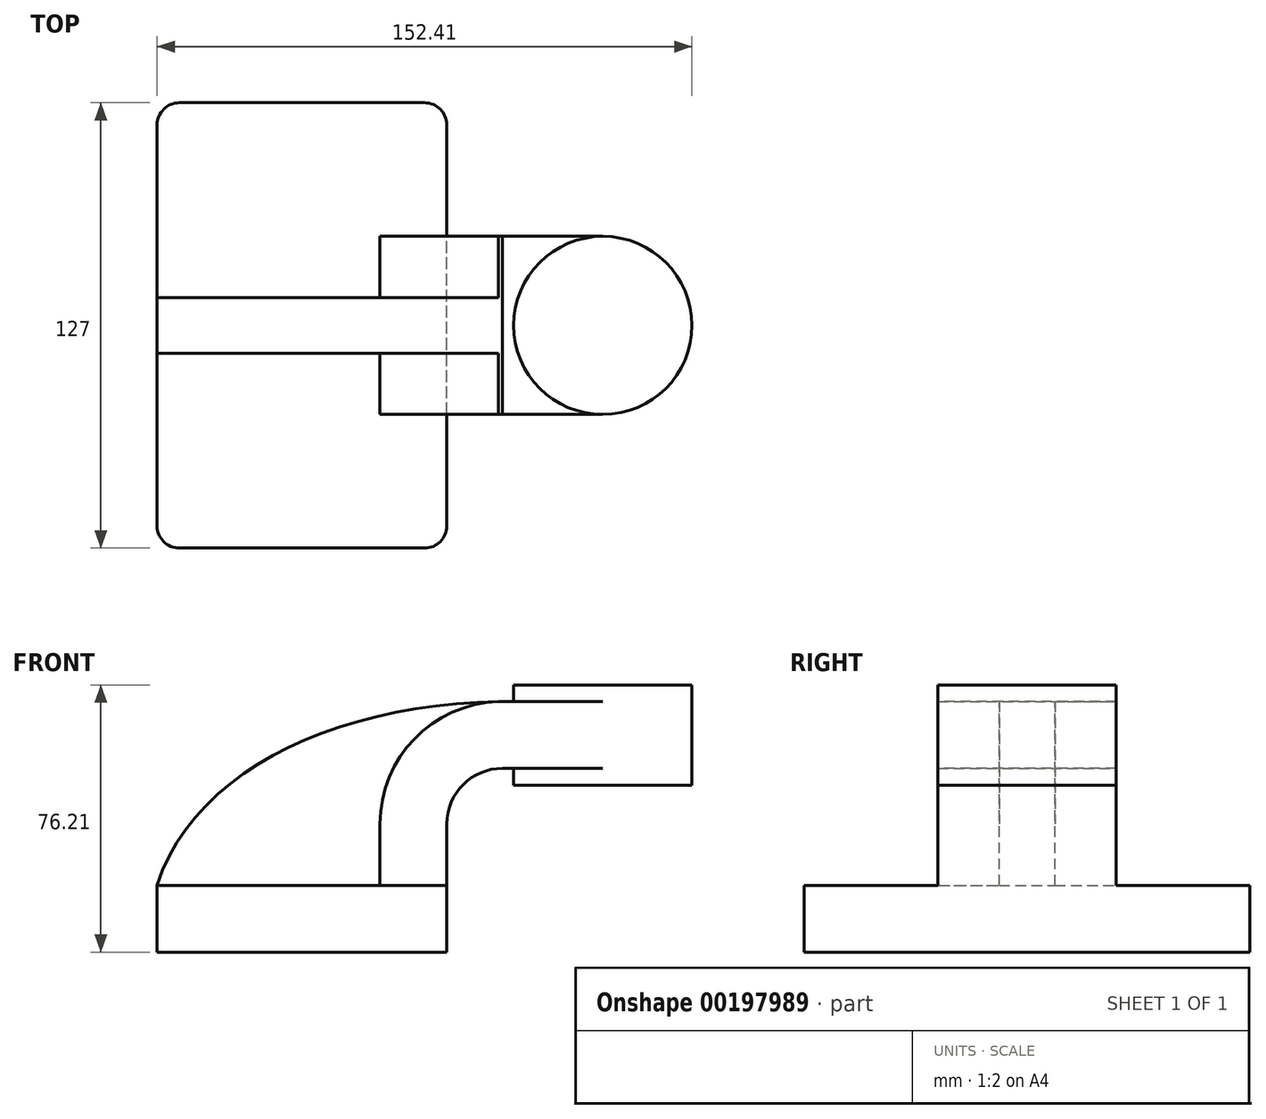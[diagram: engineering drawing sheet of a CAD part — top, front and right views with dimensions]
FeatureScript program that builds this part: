
annotation { "Feature Type Name" : "Feature", "Feature Type Description" : "" }
export const myFeature = defineFeature(function(context is Context, id is Id, definition is map)
    precondition{}
    {
        {
            var Q0;
            Q0=qCreatedBy(makeId("Front.planeOp"),FACE);
            var sketch = newSketch(context, id + "F0", { "sketchPlane" : qUnion([Q0])});
            skLineSegment(sketch, "E0.bottom", {"start": v(-41.28, 9.52) * mm, "end": v(41.28, 9.52) * mm});
            skLineSegment(sketch, "E0.top", {"start": v(-41.27, -9.53) * mm, "end": v(41.28, -9.53) * mm});
            skLineSegment(sketch, "E0.left", {"start": v(-41.28, 9.52) * mm, "end": v(-41.28, -9.53) * mm});
            skLineSegment(sketch, "E0.right", {"start": v(41.27, 9.53) * mm, "end": v(41.28, -9.52) * mm});
            skPoint(sketch, "E0.middle", {"position": v(0, 0) * mm});
            skLineSegment(sketch, "E1.bottom", {"start": v(111.12, 38.1) * mm, "end": v(60.32, 38.1) * mm});
            skLineSegment(sketch, "E1.top", {"start": v(111.12, 66.68) * mm, "end": v(60.32, 66.68) * mm});
            skLineSegment(sketch, "E1.left", {"start": v(111.12, 38.1) * mm, "end": v(111.12, 66.68) * mm});
            skLineSegment(sketch, "E1.right", {"start": v(60.32, 38.1) * mm, "end": v(60.32, 66.68) * mm});
            skPoint(sketch, "E1.middle", {"position": v(85.72, 52.39) * mm});
            skLineSegment(sketch, "E2", {"start": v(41.27, 9.53) * mm, "end": v(41.27, 27) * mm});
            skArc(sketch, "E3", {"start": v(41.27, 27) * mm, "mid": v(45.92, 38.23) * mm, "end": v(57.15, 42.88) * mm});
            skLineSegment(sketch, "E4", {"start": v(57.15, 42.88) * mm, "end": v(85.72, 42.88) * mm});
            skLineSegment(sketch, "E5.0", {"start": v(57.15, 61.93) * mm, "end": v(85.72, 61.93) * mm});
            skArc(sketch, "E5.1", {"start": v(22.22, 27) * mm, "mid": v(32.45, 51.7) * mm, "end": v(57.15, 61.93) * mm});
            skLineSegment(sketch, "E5.2", {"start": v(22.22, 9.52) * mm, "end": v(22.22, 27) * mm});
            skFitSpline(sketch, "E6", {"points": [v(-41.28, 9.53) * mm, v(57.15, 61.93) * mm], "startDerivative": vector(31.82, 99.3) * mm, "endDerivative": vector(140.95, 1.9) * mm});
            skLineSegment(sketch, "E7", {"start": v(85.72, 66.68) * mm, "end": v(85.72, 38.1) * mm});
            skSolve(sketch);
        }
        {
            var Q0;
            Q0=makeQuery(id+"F0.imprint","IMPRINT",FACE,{"disambiguationData":[TD([[makeQuery(id+"F0.imprint","IMPRINT",EDGE,{"derivedFrom":sQuery(id+"F0.wireOp",EDGE,"E0.top")}),1.0]])]});
            extrude(context, id + "F1", {"entities" : qUnion([Q0]), "endBound" : BoundingType.SYMMETRIC, "depth" : 127 * mm});
        }
        {
            var Q0;
            {var subQ1=sQuery(id+"F0.wireOp",EDGE,"E2");Q0=makeQuery(id+"F0.imprint","IMPRINT",FACE,{"disambiguationData":[TD([[makeQuery(id+"F0.imprint","IMPRINT",EDGE,{"derivedFrom":subQ1}),1.0]])]});}
            var Q1;
            {var subQ0=sQuery(id+"F0.wireOp",EDGE,"E4");var subQ1=sQuery(id+"F0.wireOp",EDGE,"E1.right");var subQ2=makeQuery(id+"F0.imprint","INTERSECT",VERTEX,{"derivedFrom":[subQ1,subQ0]});Q1=makeQuery(id+"F0.imprint","IMPRINT",FACE,{"disambiguationData":[TD([[makeQuery(id+"F0.imprint","IMPRINT",EDGE,{"disambiguationData":[TD([[subQ2,-1.0]])],"derivedFrom":subQ1}),-1.0]])]});}
            extrude(context, id + "F2", {"entities" : qUnion([Q0, Q1]), "operationType" : NewBodyOperationType.ADD, "endBound" : BoundingType.SYMMETRIC, "depth" : 50.8 * mm});
        }
        {
            var Q0;
            {var subQ3=sQuery(id+"F0.wireOp",EDGE,"E5.2");Q0=makeQuery(id+"F0.imprint","IMPRINT",FACE,{"disambiguationData":[TD([[makeQuery(id+"F0.imprint","IMPRINT",EDGE,{"derivedFrom":subQ3}),1.0]])]});}
            extrude(context, id + "F3", {"entities" : qUnion([Q0]), "operationType" : NewBodyOperationType.ADD, "endBound" : BoundingType.SYMMETRIC, "depth" : 15.88 * mm});
        }
        {
            var Q0;
            {var subQ4=sQuery(id+"F0.wireOp",EDGE,"E1.left");Q0=makeQuery(id+"F0.imprint","IMPRINT",FACE,{"disambiguationData":[TD([[makeQuery(id+"F0.imprint","IMPRINT",EDGE,{"derivedFrom":subQ4}),1.0]])]});}
            var Q1;
            Q1=sQuery(id+"F0.wireOp",EDGE,"E7");
            revolve(context, id + "F4", {"operationType" : NewBodyOperationType.ADD, "entities" : qUnion([Q0]), "axis" : qUnion([Q1]), "revolveType" : RevolveType.FULL});
        }
        {
            var Q0;
            Q0=makeQuery(id+"F1.opExtrude","CAP_EDGE",EDGE,{"disambiguationData":[OSD([sQuery(id+"F0.wireOp",EDGE,"E0.right")])],"isStart":false});
            var Q1;
            Q1=makeQuery(id+"F1.opExtrude","CAP_EDGE",EDGE,{"disambiguationData":[OSD([sQuery(id+"F0.wireOp",EDGE,"E0.left")])],"isStart":false});
            var Q2;
            Q2=makeQuery(id+"F1.opExtrude","CAP_EDGE",EDGE,{"disambiguationData":[OSD([sQuery(id+"F0.wireOp",EDGE,"E0.right")])],"isStart":true});
            var Q3;
            Q3=makeQuery(id+"F1.opExtrude","CAP_EDGE",EDGE,{"disambiguationData":[OSD([sQuery(id+"F0.wireOp",EDGE,"E0.left")])],"isStart":true});
            fillet(context, id + "F5", {"entities" : qUnion([Q0, Q1, Q2, Q3]), "radius" : 6.35 * mm, "tangentPropagation" : true, "allowEdgeOverflow" : false});
        }
    });
